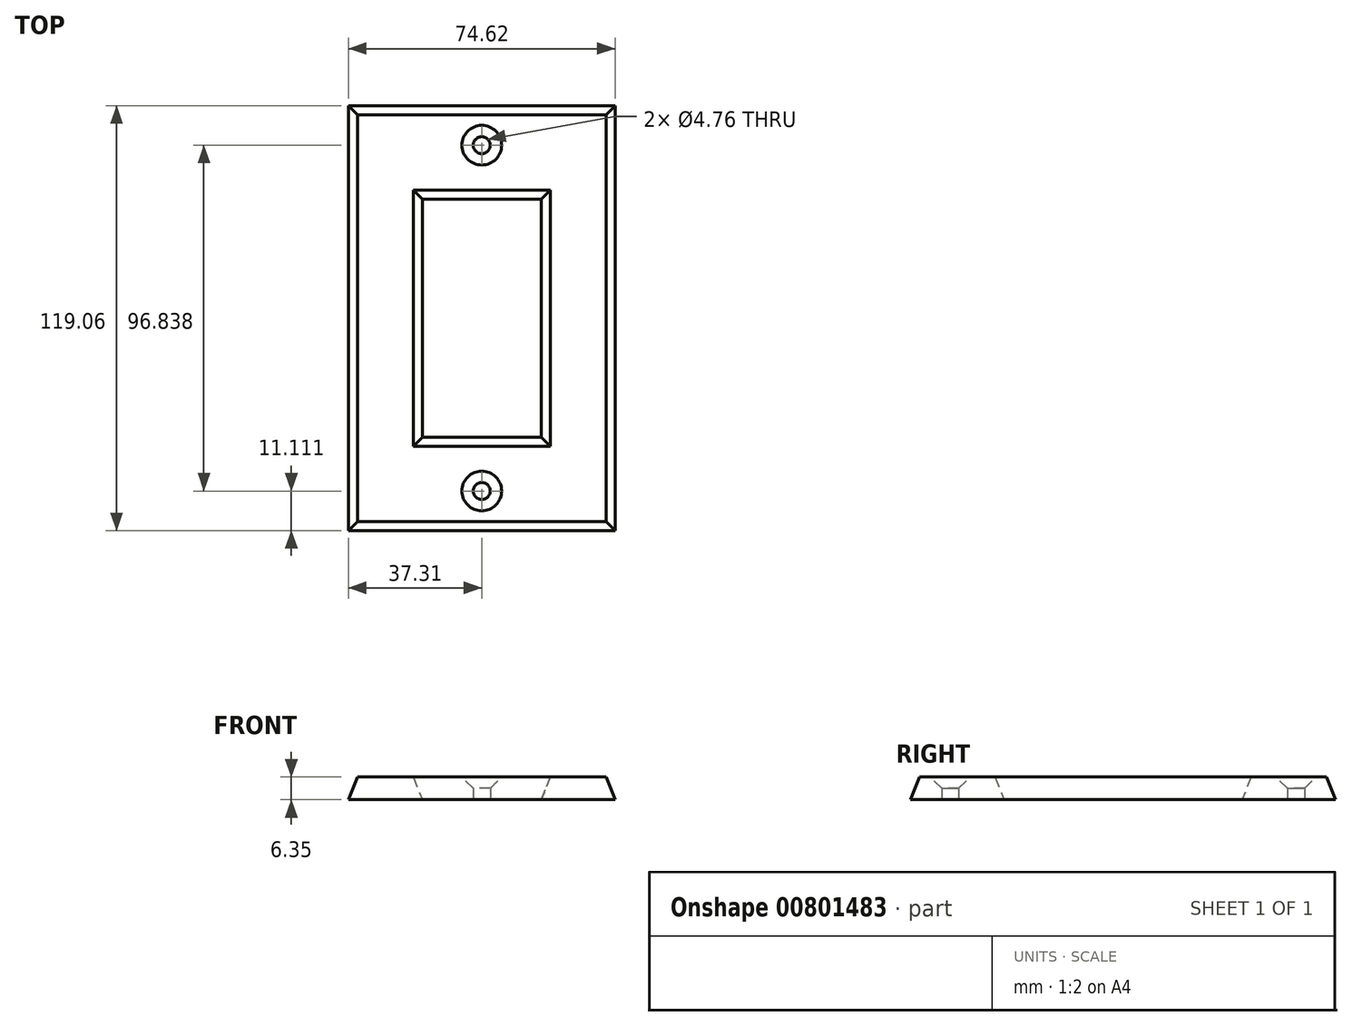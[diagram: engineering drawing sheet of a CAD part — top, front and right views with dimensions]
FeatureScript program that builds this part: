
annotation { "Feature Type Name" : "Feature", "Feature Type Description" : "" }
export const myFeature = defineFeature(function(context is Context, id is Id, definition is map)
    precondition{}
    {
        {
            var Q0;
            Q0=qCreatedBy(makeId("Top.planeOp"),FACE);
            var sketch = newSketch(context, id + "F0", { "sketchPlane" : qUnion([Q0])});
            skLineSegment(sketch, "E0.bottom", {"start": v(37.3, -59.53) * mm, "end": v(-37.3, -59.53) * mm});
            skLineSegment(sketch, "E0.top", {"start": v(37.3, 59.53) * mm, "end": v(-37.3, 59.53) * mm});
            skLineSegment(sketch, "E0.left", {"start": v(37.3, -59.53) * mm, "end": v(37.3, 59.53) * mm});
            skLineSegment(sketch, "E0.right", {"start": v(-37.3, -59.53) * mm, "end": v(-37.3, 59.53) * mm});
            skPoint(sketch, "E0.middle", {"position": v(0, 0) * mm});
            skLineSegment(sketch, "E1.bottom", {"start": v(16.67, -33.34) * mm, "end": v(-16.67, -33.34) * mm});
            skLineSegment(sketch, "E1.top", {"start": v(16.67, 33.34) * mm, "end": v(-16.67, 33.34) * mm});
            skLineSegment(sketch, "E1.left", {"start": v(16.67, -33.34) * mm, "end": v(16.67, 33.34) * mm});
            skLineSegment(sketch, "E1.right", {"start": v(-16.67, -33.34) * mm, "end": v(-16.67, 33.34) * mm});
            skLineSegment(sketch, "E2", {"start": v(0, 59.53) * mm, "end": v(0, -59.53) * mm, "construction": true});
            skCircle(sketch, "E3", {"center": v(0, 48.42) * mm, "radius": 2.38 * mm});
            skCircle(sketch, "E4", {"center": v(0, -48.42) * mm, "radius": 2.38 * mm});
            skLineSegment(sketch, "E5", {"start": v(0, 48.42) * mm, "end": v(0, -48.42) * mm, "construction": true});
            skSolve(sketch);
        }
        {
            var Q0;
            Q0 = qSketchRegion(id + "F0", true);
            extrude(context, id + "F1", {"entities" : qUnion([Q0]), "depth" : 6.35 * mm, "offsetDistance" : 25.4 * mm});
        }
        {
            var Q0;
            Q0=makeQuery(id+"F1.opExtrude","CAP_EDGE",EDGE,{"disambiguationData":[OSD([sQuery(id+"F0.wireOp",EDGE,"E1.right")])],"isStart":false});
            var Q1;
            Q1=makeQuery(id+"F1.opExtrude","CAP_EDGE",EDGE,{"disambiguationData":[OSD([sQuery(id+"F0.wireOp",EDGE,"E1.bottom")])],"isStart":false});
            var Q2;
            Q2=makeQuery(id+"F1.opExtrude","CAP_EDGE",EDGE,{"disambiguationData":[OSD([sQuery(id+"F0.wireOp",EDGE,"E1.left")])],"isStart":false});
            var Q3;
            Q3=makeQuery(id+"F1.opExtrude","CAP_EDGE",EDGE,{"disambiguationData":[OSD([sQuery(id+"F0.wireOp",EDGE,"E1.top")])],"isStart":false});
            var Q4;
            Q4=makeQuery(id+"F1.opExtrude","CAP_EDGE",EDGE,{"disambiguationData":[OSD([sQuery(id+"F0.wireOp",EDGE,"E0.top")])],"isStart":false});
            var Q5;
            Q5=makeQuery(id+"F1.opExtrude","CAP_EDGE",EDGE,{"disambiguationData":[OSD([sQuery(id+"F0.wireOp",EDGE,"E0.left")])],"isStart":false});
            var Q6;
            Q6=makeQuery(id+"F1.opExtrude","CAP_EDGE",EDGE,{"disambiguationData":[OSD([sQuery(id+"F0.wireOp",EDGE,"E0.bottom")])],"isStart":false});
            var Q7;
            Q7=makeQuery(id+"F1.opExtrude","CAP_EDGE",EDGE,{"disambiguationData":[OSD([sQuery(id+"F0.wireOp",EDGE,"E0.right")])],"isStart":false});
            chamfer(context, id + "F2", {"entities" : qUnion([Q0, Q1, Q2, Q3, Q4, Q5, Q6, Q7]), "chamferType" : ChamferType.TWO_OFFSETS, "width1" : 2.54 * mm, "oppositeDirection" : false, "width2" : 6.35 * mm, "tangentPropagation" : true});
        }
        {
            var Q0;
            Q0=makeQuery(id+"F1.opExtrude","CAP_EDGE",EDGE,{"disambiguationData":[OSD([sQuery(id+"F0.wireOp",EDGE,"E4")])],"isStart":false});
            var Q1;
            Q1=makeQuery(id+"F1.opExtrude","CAP_EDGE",EDGE,{"disambiguationData":[OSD([sQuery(id+"F0.wireOp",EDGE,"E3")])],"isStart":false});
            chamfer(context, id + "F3", {"entities" : qUnion([Q0, Q1]), "width" : 3.17 * mm, "tangentPropagation" : true});
        }
    });
